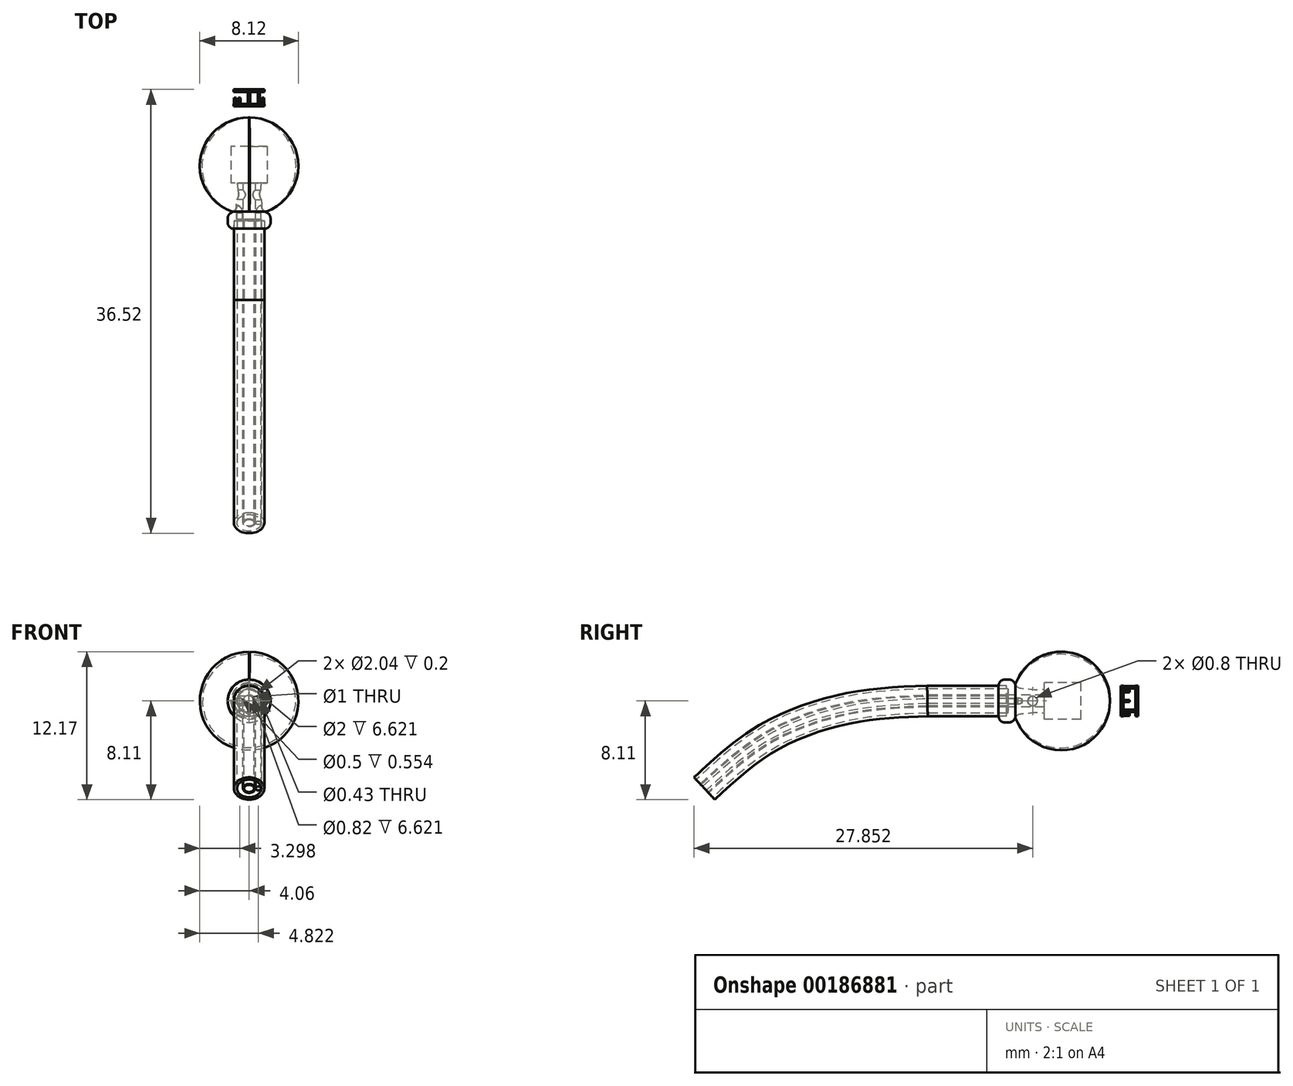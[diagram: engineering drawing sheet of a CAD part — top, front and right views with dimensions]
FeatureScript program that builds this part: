
annotation { "Feature Type Name" : "Feature", "Feature Type Description" : "" }
export const myFeature = defineFeature(function(context is Context, id is Id, definition is map)
    precondition{}
    {
        {
            var Q0;
            Q0=qCreatedBy(makeId("Front.planeOp"),FACE);
            var sketch = newSketch(context, id + "F0", { "sketchPlane" : qUnion([Q0])});
            skCircle(sketch, "E0", {"center": v(0, 0) * mm, "radius": 1 * mm});
            skCircle(sketch, "E1", {"center": v(0, 0) * mm, "radius": 1.25 * mm});
            skSolve(sketch);
        }
        {
            var Q0;
            Q0=qCreatedBy(makeId("Right.planeOp"),FACE);
            var sketch = newSketch(context, id + "F1", { "sketchPlane" : qUnion([Q0])});
            skLineSegment(sketch, "E2", {"start": v(0, 0) * mm, "end": v(-6.62, 0) * mm});
            skFitSpline(sketch, "E3", {"points": [v(-6.62, 0) * mm, v(-12.57, -0.5) * mm, v(-19.58, -2.93) * mm, v(-24.97, -7.2) * mm], "startDerivative": vector(-18.42, -0.62) * mm, "endDerivative": vector(-14.87, -13.82) * mm});
            skSolve(sketch);
        }
        {
            var Q0;
            Q0=qSketchRegion(id+"F0",true);
            var Q1;
            Q1=sQuery(id+"F1.wireOp",EDGE,"E2");
            var Q2;
            Q2=sQuery(id+"F1.wireOp",EDGE,"E3");
            sweep(context, id + "F2", {"profiles" : qUnion([Q0]), "path" : qUnion([Q1, Q2])});
        }
        {
            var Q0;
            Q0=qCreatedBy(makeId("Right.planeOp"),FACE);
            var sketch = newSketch(context, id + "F3", { "sketchPlane" : qUnion([Q0])});
            skLineSegment(sketch, "E4", {"start": v(-0.77, 1.26) * mm, "end": v(-0.77, 1.76) * mm});
            skLineSegment(sketch, "E5", {"start": v(-0.77, 1.76) * mm, "end": v(0, 1.76) * mm});
            skLineSegment(sketch, "E6", {"start": v(0, 1.76) * mm, "end": v(0.43, 1.76) * mm});
            skLineSegment(sketch, "E7", {"start": v(3, 1) * mm, "end": v(3, 0.5) * mm});
            skLineSegment(sketch, "E8", {"start": v(3, 0.5) * mm, "end": v(0, 0.5) * mm});
            skLineSegment(sketch, "E9", {"start": v(0, 0.5) * mm, "end": v(0, 1.25) * mm});
            skLineSegment(sketch, "E10", {"start": v(0, 1.25) * mm, "end": v(-0.77, 1.26) * mm});
            skLineSegment(sketch, "E11", {"start": v(0, 0) * mm, "end": v(5.82, 0) * mm, "construction": true});
            skFitSpline(sketch, "E12", {"points": [v(0.43, 1.76) * mm, v(1.27, 1.04) * mm, v(3, 1) * mm], "startDerivative": vector(1.9, -5.12) * mm, "endDerivative": vector(3.74, 0.83) * mm});
            skSolve(sketch);
        }
        {
            var Q0;
            Q0=makeQuery(id+"F3.imprint","IMPRINT",FACE,{"disambiguationData":[TD([[makeQuery(id+"F3.imprint","IMPRINT",EDGE,{"derivedFrom":sQuery(id+"F3.wireOp",EDGE,"E4")}),-1.0]])]});
            var Q1;
            Q1=sQuery(id+"F3.wireOp",EDGE,"E11");
            revolve(context, id + "F4", {"operationType" : NewBodyOperationType.ADD, "entities" : qUnion([Q0]), "axis" : qUnion([Q1]), "revolveType" : RevolveType.FULL});
        }
        {
            var Q0;
            Q0=makeQuery(id+"F4.opRevolve","SWEPT_FACE",FACE,{"disambiguationData":[OSD([sQuery(id+"F3.wireOp",EDGE,"E5"),sQuery(id+"F3.wireOp",EDGE,"E6")])]});
            fillet(context, id + "F5", {"entities" : qUnion([Q0]), "radius" : 0.5 * mm, "tangentPropagation" : true, "allowEdgeOverflow" : false});
        }
        {
            var Q0;
            Q0=qCreatedBy(makeId("Front.planeOp"),FACE);
            cPlane(context, id + "F6", {"entities" : qUnion([Q0]), "cplaneType" : CPlaneType.OFFSET, "offset" : 9.5 * mm, "oppositeDirection" : true, "width" : 152.4 * mm, "height" : 152.4 * mm});
        }
        {
            var Q0;
            Q0=qCreatedBy(id+"F6.planeOp",FACE);
            var sketch = newSketch(context, id + "F7", { "sketchPlane" : qUnion([Q0])});
            skCircle(sketch, "E13", {"center": v(0, 0) * mm, "radius": 1.26 * mm});
            skCircle(sketch, "E14", {"center": v(0, 0) * mm, "radius": 1.02 * mm});
            skSolve(sketch);
        }
        {
            var Q0;
            Q0=qCreatedBy(id+"F6.planeOp",FACE);
            cPlane(context, id + "F8", {"entities" : qUnion([Q0]), "cplaneType" : CPlaneType.OFFSET, "offset" : 0.5 * mm, "oppositeDirection" : true, "width" : 152.4 * mm, "height" : 152.4 * mm});
        }
        {
            var Q0;
            Q0=makeQuery(id+"F7.imprint","IMPRINT",FACE,{"disambiguationData":[TD([[makeQuery(id+"F7.imprint","IMPRINT",EDGE,{"derivedFrom":sQuery(id+"F7.wireOp",EDGE,"E13")}),1.0]])]});
            extrude(context, id + "F9", {"entities" : qUnion([Q0]), "depth" : 0.2 * mm});
        }
        {
            var Q0;
            Q0=qCreatedBy(id+"F6.planeOp",FACE);
            var sketch = newSketch(context, id + "F10", { "sketchPlane" : qUnion([Q0])});
            skCircle(sketch, "E15", {"center": v(0, 1.14) * mm, "radius": 0.1 * mm});
            skSolve(sketch);
        }
        {
            var Q0;
            Q0=makeQuery(id+"F10.imprint","IMPRINT",FACE,{"disambiguationData":[TD([[makeQuery(id+"F10.imprint","IMPRINT",EDGE,{"derivedFrom":sQuery(id+"F10.wireOp",EDGE,"E15")}),1.0]])]});
            var Q1;
            Q1=sQuery(id+"F10.wireOp",EDGE,"E15");
            extrude(context, id + "F11", {"entities" : qUnion([Q0]), "operationType" : NewBodyOperationType.ADD, "surfaceEntities" : qUnion([Q1]), "oppositeDirection" : true, "depth" : 0.5 * mm});
        }
        {
            var Q0;
            Q0=makeQuery(id+"F9.opExtrude","SWEPT_BODY",BODY,{"disambiguationData":[OSD([sQuery(id+"F7.wireOp",EDGE,"E13"),sQuery(id+"F7.wireOp",EDGE,"E14")])]});
            var Q1;
            Q1=makeQuery(id+"F9.opExtrude","CAP_EDGE",EDGE,{"disambiguationData":[OSD([sQuery(id+"F7.wireOp",EDGE,"E14")])],"isStart":true});
            circularPattern(context, id + "F12", {"operationType" : NewBodyOperationType.ADD, "entities" : qUnion([Q0]), "axis" : qUnion([Q1]), "angle" : 360 * degree, "instanceCount" : 8, "equalSpace" : true});
        }
        {
            var Q0;
            Q0=makeQuery(id+"F9.opExtrude","SWEPT_BODY",BODY,{"disambiguationData":[OSD([sQuery(id+"F7.wireOp",EDGE,"E13"),sQuery(id+"F7.wireOp",EDGE,"E14")])]});
            var Q1;
            Q1=makeQuery(id+"F12.opPattern","COPY",BODY,{"derivedFrom":makeQuery(id+"F9.opExtrude","SWEPT_BODY",BODY,{"disambiguationData":[OSD([sQuery(id+"F7.wireOp",EDGE,"E13"),sQuery(id+"F7.wireOp",EDGE,"E14")])]}),"instanceName":"5"});
            var Q2;
            Q2=qCreatedBy(id+"F8.planeOp",FACE);
            mirror(context, id + "F13", {"operationType" : NewBodyOperationType.ADD, "entities" : qUnion([Q0, Q1]), "mirrorPlane" : qUnion([Q2])});
        }
        {
            var Q0;
            Q0=qCreatedBy(makeId("Right.planeOp"),FACE);
            var sketch = newSketch(context, id + "F14", { "sketchPlane" : qUnion([Q0])});
            skLineSegment(sketch, "E16", {"start": v(10.95, 0) * mm, "end": v(0, 0) * mm, "construction": true});
            skArc(sketch, "E17", {"start": v(8.4, 0) * mm, "mid": v(5.11, 4) * mm, "end": v(0.63, 1.4) * mm});
            skArc(sketch, "E18", {"start": v(8.4, 0) * mm, "mid": v(5.08, 3.79) * mm, "end": v(0.63, 1.4) * mm});
            skSolve(sketch);
        }
        {
            var Q0;
            Q0=makeQuery(id+"F14.imprint","IMPRINT",FACE,{"disambiguationData":[TD([[makeQuery(id+"F14.imprint","IMPRINT",EDGE,{"derivedFrom":sQuery(id+"F14.wireOp",EDGE,"E17")}),1.0]])]});
            var Q1;
            Q1=qConstructionFilter(qBodyType(qCreatedBy(id+"F14",EDGE),BodyType.WIRE),ConstructionObject.NO);
            var Q2;
            Q2=sQuery(id+"F14.wireOp",EDGE,"E16");
            revolve(context, id + "F15", {"entities" : qUnion([Q0]), "surfaceEntities" : qUnion([Q1]), "axis" : qUnion([Q2]), "revolveType" : RevolveType.ONE_DIRECTION, "angle" : 359 * degree});
        }
        {
            var Q0;
            Q0=qCreatedBy(makeId("Right.planeOp"),FACE);
            cPlane(context, id + "F16", {"entities" : qUnion([Q0]), "cplaneType" : CPlaneType.OFFSET, "offset" : 1 * mm, "oppositeDirection" : true, "width" : 152.4 * mm, "height" : 152.4 * mm});
        }
        {
            var Q0;
            Q0=qCreatedBy(id+"F16.planeOp",FACE);
            var sketch = newSketch(context, id + "F17", { "sketchPlane" : qUnion([Q0])});
            skCircle(sketch, "E19", {"center": v(2.03, 0) * mm, "radius": 0.5 * mm});
            skCircle(sketch, "E20", {"center": v(2.03, 0) * mm, "radius": 0.36 * mm});
            skSolve(sketch);
        }
        {
            var Q0;
            Q0=sQuery(id+"F17.wireOp",VERTEX,"E19.center");
            var Q1;
            Q1=makeQuery(id+"F2.opSweep","SWEPT_BODY",BODY,{"disambiguationData":[OSD([sQuery(id+"F0.wireOp",EDGE,"E0"),sQuery(id+"F0.wireOp",EDGE,"E1"),sQuery(id+"F1.wireOp",EDGE,"E3")])]});
            hole(context, id + "F18", {"style" : HoleStyle.SIMPLE, "endStyle" : HoleEndStyle.BLIND, "oppositeDirection" : true, "holeDiameter" : 0.8 * mm, "holeDepth" : 1 * mm, "startFromSketch" : true, "locations" : qUnion([Q0]), "scope" : qUnion([Q1])});
        }
        {
            var Q0;
            Q0=qCreatedBy(makeId("Right.planeOp"),FACE);
            cPlane(context, id + "F19", {"entities" : qUnion([Q0]), "cplaneType" : CPlaneType.OFFSET, "offset" : 1 * mm, "width" : 152.4 * mm, "height" : 152.4 * mm});
        }
        {
            var Q0;
            Q0=qCreatedBy(id+"F19.planeOp",FACE);
            var sketch = newSketch(context, id + "F20", { "sketchPlane" : qUnion([Q0])});
            skCircle(sketch, "E21", {"center": v(2.03, 0) * mm, "radius": 0.5 * mm});
            skSolve(sketch);
        }
        {
            var Q0;
            Q0=sQuery(id+"F20.wireOp",VERTEX,"E21.center");
            var Q1;
            Q1=makeQuery(id+"F2.opSweep","SWEPT_BODY",BODY,{"disambiguationData":[OSD([sQuery(id+"F0.wireOp",EDGE,"E0"),sQuery(id+"F0.wireOp",EDGE,"E1"),sQuery(id+"F1.wireOp",EDGE,"E3")])]});
            hole(context, id + "F21", {"style" : HoleStyle.SIMPLE, "endStyle" : HoleEndStyle.BLIND, "holeDiameter" : 0.8 * mm, "holeDepth" : 1 * mm, "startFromSketch" : true, "locations" : qUnion([Q0]), "scope" : qUnion([Q1])});
        }
        {
            var Q0;
            Q0=qCreatedBy(makeId("Front.planeOp"),FACE);
            cPlane(context, id + "F22", {"entities" : qUnion([Q0]), "cplaneType" : CPlaneType.OFFSET, "offset" : 3 * mm, "oppositeDirection" : true, "width" : 152.4 * mm, "height" : 152.4 * mm});
        }
        {
            var Q0;
            Q0=qCreatedBy(id+"F22.planeOp",FACE);
            var sketch = newSketch(context, id + "F23", { "sketchPlane" : qUnion([Q0])});
            skCircle(sketch, "E22", {"center": v(0, 0) * mm, "radius": 1.5 * mm});
            skSolve(sketch);
        }
        {
            var Q0;
            Q0 = qSketchRegion(id + "F23", true);
            extrude(context, id + "F24", {"entities" : qUnion([Q0]), "oppositeDirection" : true, "depth" : 3 * mm});
        }
        {
            var Q0;
            Q0=qCreatedBy(makeId("Front.planeOp"),FACE);
            var sketch = newSketch(context, id + "F25", { "sketchPlane" : qUnion([Q0])});
            skCircle(sketch, "E23", {"center": v(0, 0) * mm, "radius": 0.5 * mm});
            skCircle(sketch, "E24", {"center": v(0, 0) * mm, "radius": 0.4 * mm});
            skSolve(sketch);
        }
        {
            var Q0;
            Q0=makeQuery(id+"F25.imprint","IMPRINT",FACE,{"disambiguationData":[TD([[makeQuery(id+"F25.imprint","IMPRINT",EDGE,{"derivedFrom":sQuery(id+"F25.wireOp",EDGE,"E23")}),1.0]])]});
            var Q1;
            Q1 = qConstructionFilter(qBodyType(qCreatedBy(id + "F1" ,EDGE), BodyType.WIRE), ConstructionObject.NO);
            sweep(context, id + "F26", {"profiles" : qUnion([Q0]), "path" : qUnion([Q1])});
        }
        {
            var Q0;
            Q0=qCreatedBy(makeId("Top.planeOp"),FACE);
            var sketch = newSketch(context, id + "F27", { "sketchPlane" : qUnion([Q0])});
            skLineSegment(sketch, "E25", {"start": v(-0.75, 0) * mm, "end": v(-0.75, 0.55) * mm});
            skFitSpline(sketch, "E26", {"points": [v(-0.75, 0.55) * mm, v(-1.08, 0.98) * mm], "startDerivative": vector(-0.02, 0.43) * mm, "endDerivative": vector(-0.7, 0.19) * mm});
            skLineSegment(sketch, "E27.MirrorCS", {"start": v(0.75, 0) * mm, "end": v(0.75, 0.55) * mm});
            skFitSpline(sketch, "E28.MirrorCS", {"points": [v(0.75, 0.55) * mm, v(1.08, 0.98) * mm], "startDerivative": vector(0.02, 0.43) * mm, "endDerivative": vector(0.7, 0.19) * mm});
            skSolve(sketch);
        }
        {
            var Q0;
            Q0=qCreatedBy(makeId("Front.planeOp"),FACE);
            var sketch = newSketch(context, id + "F28", { "sketchPlane" : qUnion([Q0])});
            skCircle(sketch, "E29", {"center": v(-0.76, 0) * mm, "radius": 0.25 * mm});
            skCircle(sketch, "E30", {"center": v(-0.76, 0) * mm, "radius": 0.22 * mm});
            skCircle(sketch, "E31.MirrorC", {"center": v(0.76, 0) * mm, "radius": 0.22 * mm});
            skCircle(sketch, "E32.MirrorC", {"center": v(0.76, 0) * mm, "radius": 0.25 * mm});
            skSolve(sketch);
        }
        {
            var Q0;
            Q0=makeQuery(id+"F28.imprint","IMPRINT",FACE,{"disambiguationData":[TD([[makeQuery(id+"F28.imprint","IMPRINT",EDGE,{"derivedFrom":sQuery(id+"F28.wireOp",EDGE,"E29")}),1.0]])]});
            var Q1;
            Q1=sQuery(id+"F27.wireOp",EDGE,"E25");
            var Q2;
            Q2=sQuery(id+"F27.wireOp",EDGE,"E26");
            sweep(context, id + "F29", {"operationType" : NewBodyOperationType.REMOVE, "profiles" : qUnion([Q0]), "path" : qUnion([Q1, Q2])});
        }
        {
            var Q0;
            Q0=makeQuery(id+"F28.imprint","IMPRINT",FACE,{"disambiguationData":[TD([[makeQuery(id+"F28.imprint","IMPRINT",EDGE,{"derivedFrom":sQuery(id+"F28.wireOp",EDGE,"E31.MirrorC")}),1.0]])]});
            var Q1;
            Q1=sQuery(id+"F27.wireOp",EDGE,"E27.MirrorCS");
            var Q2;
            Q2=sQuery(id+"F27.wireOp",EDGE,"E28.MirrorCS");
            sweep(context, id + "F30", {"operationType" : NewBodyOperationType.REMOVE, "profiles" : qUnion([Q0]), "path" : qUnion([Q1, Q2])});
        }
        {
            var Q0;
            Q0=qCreatedBy(makeId("Right.planeOp"),FACE);
            cPlane(context, id + "F31", {"entities" : qUnion([Q0]), "cplaneType" : CPlaneType.OFFSET, "offset" : 0.76 * mm, "width" : 152.4 * mm, "height" : 152.4 * mm});
        }
        {
            var Q0;
            Q0=qCreatedBy(id+"F31.planeOp",FACE);
            var sketch = newSketch(context, id + "F32", { "sketchPlane" : qUnion([Q0])});
            skLineSegment(sketch, "E33", {"start": v(0, 0) * mm, "end": v(-6.62, 0) * mm});
            skFitSpline(sketch, "E34", {"points": [v(-6.62, 0) * mm, v(-12.57, -0.5) * mm, v(-19.58, -2.93) * mm, v(-24.97, -7.2) * mm], "startDerivative": vector(-18.42, -0.62) * mm, "endDerivative": vector(-14.87, -13.82) * mm});
            skSolve(sketch);
        }
        {
            var Q0;
            Q0=makeQuery(id+"F28.imprint","IMPRINT",FACE,{"disambiguationData":[TD([[makeQuery(id+"F28.imprint","IMPRINT",EDGE,{"derivedFrom":sQuery(id+"F28.wireOp",EDGE,"E31.MirrorC")}),1.0]])]});
            var Q1;
            Q1 = qConstructionFilter(qBodyType(qCreatedBy(id + "F32" ,EDGE), BodyType.WIRE), ConstructionObject.NO);
            sweep(context, id + "F33", {"operationType" : NewBodyOperationType.ADD, "profiles" : qUnion([Q0]), "path" : qUnion([Q1])});
        }
    });
